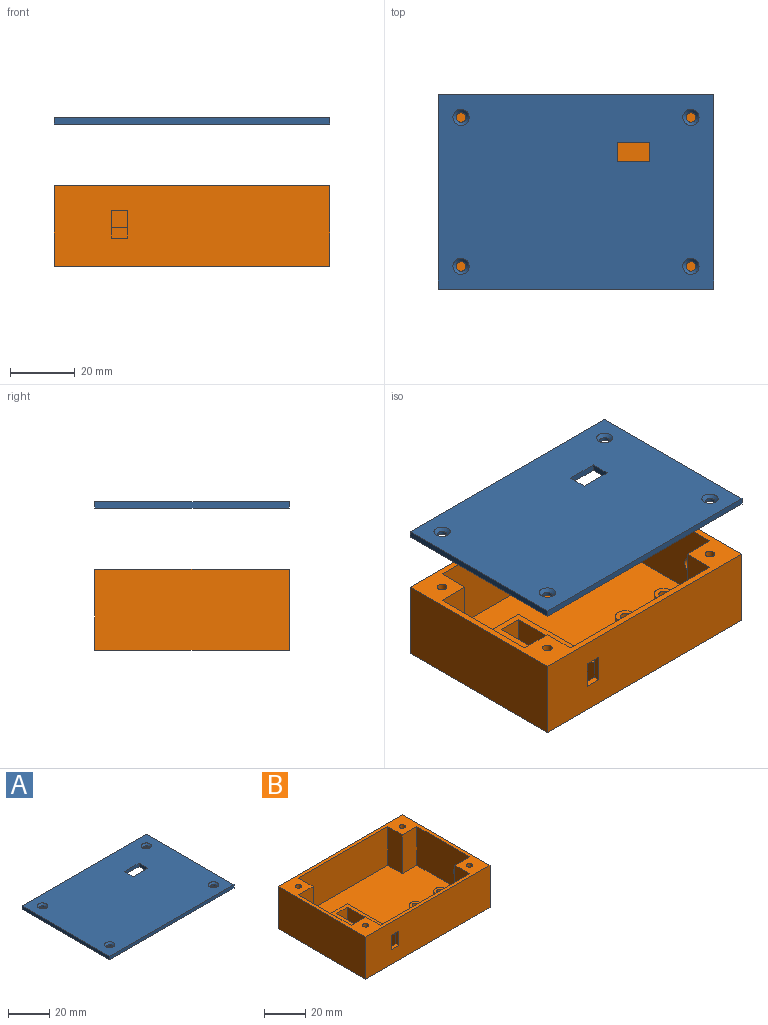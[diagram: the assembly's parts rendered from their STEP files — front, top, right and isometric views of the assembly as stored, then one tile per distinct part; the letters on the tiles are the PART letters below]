
ASSEMBLY  parts=2 mates=1
PART A: 18 faces, bbox 85x60x2 mm
  f0: plane 85x60mm, normal (0,0,1), area 4961.5mm2, adj f2,f3,f4,f5,f10,f11,f12,f13
  f1: plane 85x60mm, normal (0,0,-1), area 5011.7mm2, adj f2,f3,f4,f5,f6,f7,f8,f9
  f2: plane 85x2mm, normal (0,1,0), area 170mm2, adj f0,f1,f3,f5
  f3: plane 60x2mm, normal (-1,0,0), area 120mm2, adj f0,f1,f2,f4
  f4: plane 85x2mm, normal (0,-1,0), area 170mm2, adj f0,f1,f3,f5
  f5: plane 60x2mm, normal (1,0,0), area 120mm2, adj f0,f1,f2,f4
  f6: cylinder r=1.5mm len=3mm, axis (0,0,1), area 9.4mm2, adj f1,f16
  f7: cylinder r=1.5mm len=3mm, axis (0,0,1), area 9.4mm2, adj f1,f14
  f8: cylinder r=1.5mm len=3mm, axis (0,0,1), area 9.4mm2, adj f1,f15
  f9: cylinder r=1.5mm len=3mm, axis (0,0,1), area 9.4mm2, adj f1,f17
  f10: plane 6x2mm, normal (-1,0,0), area 12mm2, adj f0,f1,f11,f13
  f11: plane 10x2mm, normal (0,-1,0), area 20mm2, adj f0,f1,f10,f12
  f12: plane 6x2mm, normal (1,0,0), area 12mm2, adj f0,f1,f11,f13
  f13: plane 10x2mm, normal (0,1,0), area 20mm2, adj f0,f1,f10,f12
  f14: cone r=1.5mm half-angle=45deg, axis (0,0,1), area 17.8mm2, adj f0,f7
  f15: cone r=1.5mm half-angle=45deg, axis (0,0,1), area 17.8mm2, adj f0,f8
  f16: cone r=1.5mm half-angle=45deg, axis (0,0,1), area 17.8mm2, adj f0,f6
  f17: cone r=1.5mm half-angle=45deg, axis (0,0,1), area 17.8mm2, adj f0,f9
PART B: 48 faces, bbox 85x60x25 mm
  f0: plane 61x23mm, normal (0,1,0), area 1340.5mm2, adj f1,f9,f14,f16,f27,f28,f29,f30
  f1: plane 81x56mm, normal (0,0,1), area 3942.5mm2, adj f0,f3,f4,f5,f11,f12,f13,f14
  f2: plane 85x25mm, normal (0,-1,0), area 2082.5mm2, adj f6,f8,f9,f10,f27,f28,f29,f30
  f3: plane 61x23mm, normal (0,-1,0), area 1403mm2, adj f1,f9,f12,f18
  f4: plane 36x23mm, normal (-1,0,0), area 799.7mm2, adj f1,f9,f15,f17,f31
  f5: plane 36x23mm, normal (1,0,0), area 828mm2, adj f1,f9,f11,f13
  f6: plane 60x25mm, normal (1,0,0), area 1471.7mm2, adj f2,f7,f9,f10,f31
  f7: plane 85x25mm, normal (0,1,0), area 2125mm2, adj f6,f8,f9,f10
  f8: plane 60x25mm, normal (-1,0,0), area 1500mm2, adj f2,f7,f9,f10
  f9: plane 85x60mm, normal (0,0,1), area 935.7mm2, adj f0,f2,f3,f4,f5,f6,f7,f8
  f10: plane 85x60mm, normal (0,0,-1), area 5100mm2, adj f2,f6,f7,f8
  f11: plane 23x10mm, normal (0,-1,0), area 230mm2, adj f1,f5,f9,f12
  f12: plane 23x10mm, normal (1,0,0), area 230mm2, adj f1,f3,f9,f11
  f13: plane 23x10mm, normal (0,1,0), area 230mm2, adj f1,f5,f9,f14
  f14: plane 23x10mm, normal (1,0,0), area 230mm2, adj f0,f1,f9,f13
  f15: plane 23x10mm, normal (0,1,0), area 230mm2, adj f1,f4,f9,f16
  f16: plane 23x10mm, normal (-1,0,0), area 230mm2, adj f0,f1,f9,f15
  f17: plane 23x10mm, normal (0,-1,0), area 230mm2, adj f1,f4,f9,f18
  f18: plane 23x10mm, normal (-1,0,0), area 230mm2, adj f1,f3,f9,f17
  f19: cylinder r=1.5mm len=12mm, axis (0,0,1), area 113.1mm2, adj f9,f20
  f20: plane 3x3mm, normal (0,0,1), area 7.1mm2, adj f19
  f21: cylinder r=1.5mm len=12mm, axis (0,0,1), area 113.1mm2, adj f9,f22
  f22: plane 3x3mm, normal (0,0,1), area 7.1mm2, adj f21
  f23: cylinder r=1.5mm len=12mm, axis (0,0,1), area 113.1mm2, adj f9,f24
  f24: plane 3x3mm, normal (0,0,1), area 7.1mm2, adj f23
  f25: cylinder r=1.5mm len=12mm, axis (0,0,1), area 113.1mm2, adj f9,f26
  f26: plane 3x3mm, normal (0,0,1), area 7.1mm2, adj f25
  f27: plane 5x2mm, normal (0,0,1), area 10mm2, adj f0,f2,f28,f30
  f28: plane 8.5x2mm, normal (-1,0,0), area 17mm2, adj f0,f2,f27,f29
  f29: plane 5x2mm, normal (0,0,-1), area 10mm2, adj f0,f2,f28,f30
  f30: plane 8.5x2mm, normal (1,0,0), area 17mm2, adj f0,f2,f27,f29
  f31: cylinder r=3mm len=6mm, axis (1,0,0), area 37.7mm2, adj f4,f6
  f32: cylinder r=1.5mm len=5mm, axis (0,0,-1), area 47.1mm2, adj f34,f35
  f33: cylinder r=3mm len=6mm, axis (0,0,-1), area 94.2mm2, adj f1,f34
  f34: plane 6x6mm, normal (0,0,1), area 21.2mm2, adj f32,f33
  f35: plane 3x3mm, normal (0,0,1), area 7.1mm2, adj f32
  f36: cylinder r=1.5mm len=5mm, axis (0,0,-1), area 47.1mm2, adj f38,f39
  f37: cylinder r=3mm len=6mm, axis (0,0,-1), area 94.2mm2, adj f1,f38
  f38: plane 6x6mm, normal (0,0,1), area 21.2mm2, adj f36,f37
  f39: plane 3x3mm, normal (0,0,1), area 7.1mm2, adj f36
  f40: plane 37x10mm, normal (1,0,0), area 370mm2, adj f0,f1,f41,f47
  f41: plane 11.5x10mm, normal (0,1,0), area 115mm2, adj f1,f40,f42,f47
  f42: plane 24x10mm, normal (-1,0,0), area 240mm2, adj f1,f41,f43,f47
  f43: plane 10x2mm, normal (0,-1,0), area 20mm2, adj f1,f42,f44,f47
  f44: plane 22x10mm, normal (1,0,0), area 220mm2, adj f1,f43,f45,f47
  f45: plane 10x7.5mm, normal (0,-1,0), area 75mm2, adj f1,f44,f46,f47
  f46: plane 35x10mm, normal (-1,0,0), area 350mm2, adj f0,f1,f45,f47
  f47: plane 37x11.5mm, normal (0,0,1), area 137mm2, adj f0,f40,f41,f42,f43,f44,f45,f46
PLACE A t=(-283.75,-41.2,52.69)mm
PLACE B t=(-141.87,-24.03,8.74)mm fixed
MATE slider B.f23 <-> A.f8  axis (0,0,1) through (-106.37,-47.03,33.74)mm
